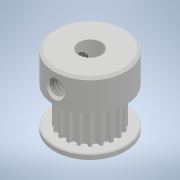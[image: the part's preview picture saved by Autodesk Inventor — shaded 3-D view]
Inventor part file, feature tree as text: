
AUTODESK INVENTOR PART (.ipt)
format: ipt  version: 2022.2 (Build 262287010, 287A)  size: 324,608 bytes
history: native  units: mm
features: chamfer x3, sketch x3, extrude x2, pattern_circular x2, revolve x1, thread x1, projected_geometry x1
ambient origin geometry x8: Origin, YZ Plane, XZ Plane, XY Plane, X Axis, Y Axis, Z Axis, Center Point
bodies: Solid1 (feature_tree)
feature tree (13):
  revolve  "Revolution1"  Angle=90.0deg
  extrude  "Extrusion1"  Depth=1.3mm
  pattern_circular  "Circular Pattern1"  [2 undecoded]
  chamfer  "Chamfer1"  Distance=7.4mm
  extrude  "Extrusion2"  Depth=10.0mm
  chamfer  "Chamfer2"  Distance=6.0mm
  thread  "Thread1"  [1 undecoded]
  pattern_circular  "Circular Pattern2"  Angle=90.0deg  [1 undecoded]
  chamfer  "Chamfer3"  Distance=2.0mm
  sketch  "Sketch1"  dims[d0=15.0mm d1=90.0deg]
  sketch  "Sketch3"  dims[d2=8.0mm d3=1.3mm]
  sketch  "Sketch4"  dims[d4=7.3mm d5=16.0mm d6=7.4mm d7=7.975mm d8=6.0mm d9=2.5mm d10=90.0deg d11=2.0mm d12=1.11mm d27=1.38mm d28=0.75mm d29=1.11mm d31=0.4mm d33=0.555mm d34=1.0mm d35=2.0mm d36=1.0mm d38=0.15mm d39=0.63mm d40=2.0mm d43=0.15mm d45=0.519649mm d46=10.0mm d47=0.0mm d48=200.0mm d49=360.0deg d51=0.5mm d52=2.0mm d53=45.0deg d54=3.3mm d55=7.4mm d56=3.7mm d57=10.0mm d58=0.0mm d59=0.5mm d60=2.0mm d61=45.0deg d62=10.0mm d63=0.0mm d64=20.0mm d65=90.0deg d67=0.2mm d68=2.0mm d69=45.0deg]
  projected_geometry  "Project Cut Edges2"
note: 4 required parameter values undecoded (feature->parameter linkage not recoverable at this tier; creation-order binding heuristic only, values carry confidence <= 0.55)
